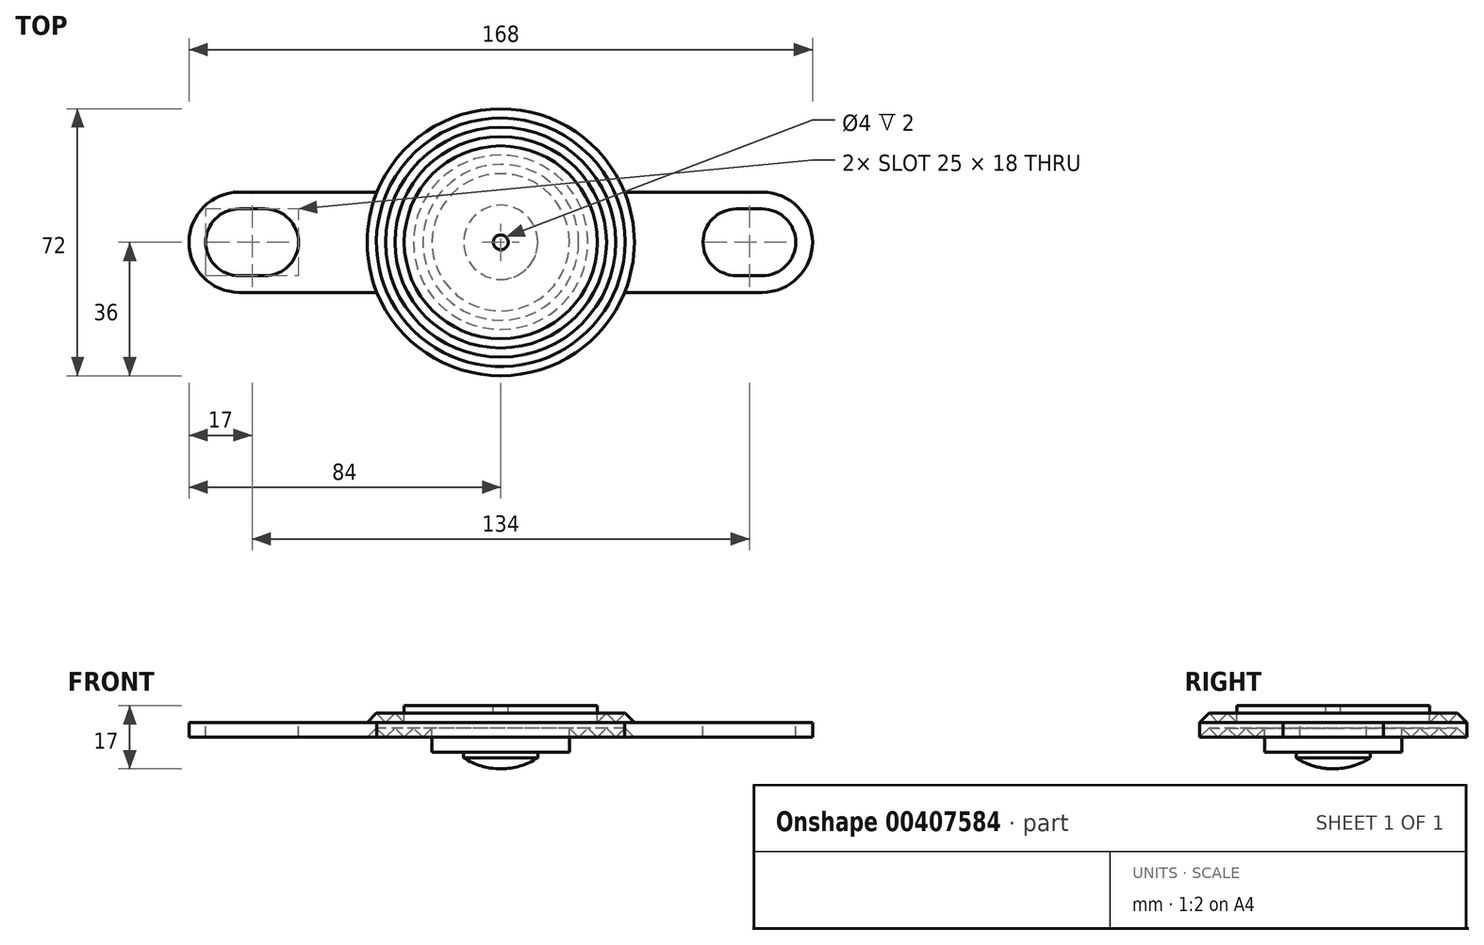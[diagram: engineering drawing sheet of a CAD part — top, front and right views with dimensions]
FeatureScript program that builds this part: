
annotation { "Feature Type Name" : "Feature", "Feature Type Description" : "" }
export const myFeature = defineFeature(function(context is Context, id is Id, definition is map)
    precondition{}
    {
        {
            var Q0;
            Q0=qCreatedBy(makeId("Right.planeOp"),FACE);
            var sketch = newSketch(context, id + "F0", { "sketchPlane" : qUnion([Q0])});
            skLineSegment(sketch, "E0", {"start": v(0, 21.06) * mm, "end": v(0, -33.67) * mm, "construction": true});
            skLineSegment(sketch, "E1", {"start": v(2, 0) * mm, "end": v(26, 0) * mm});
            skLineSegment(sketch, "E2", {"start": v(26, 0) * mm, "end": v(26, -4.5) * mm});
            skLineSegment(sketch, "E3", {"start": v(26, -4.5) * mm, "end": v(28.5, -2) * mm});
            skLineSegment(sketch, "E4", {"start": v(28.5, -2) * mm, "end": v(31, -4.5) * mm});
            skLineSegment(sketch, "E5", {"start": v(31, -4.5) * mm, "end": v(33.5, -2) * mm});
            skLineSegment(sketch, "E6", {"start": v(33.5, -2) * mm, "end": v(36, -4.5) * mm});
            skLineSegment(sketch, "E7", {"start": v(36, -4.5) * mm, "end": v(36, -8.5) * mm});
            skLineSegment(sketch, "E8", {"start": v(36, -8.5) * mm, "end": v(33.5, -6) * mm});
            skLineSegment(sketch, "E9", {"start": v(33.5, -6) * mm, "end": v(31, -8.5) * mm});
            skLineSegment(sketch, "E10", {"start": v(31, -8.5) * mm, "end": v(28.5, -6) * mm});
            skLineSegment(sketch, "E11", {"start": v(28.5, -6) * mm, "end": v(26, -8.5) * mm});
            skLineSegment(sketch, "E12", {"start": v(26, -8.5) * mm, "end": v(23.5, -6) * mm});
            skLineSegment(sketch, "E13", {"start": v(23.5, -6) * mm, "end": v(21, -8.5) * mm});
            skLineSegment(sketch, "E14", {"start": v(21, -8.5) * mm, "end": v(18.5, -6) * mm});
            skLineSegment(sketch, "E15", {"start": v(18.5, -6) * mm, "end": v(18.5, -12.5) * mm});
            skLineSegment(sketch, "E16", {"start": v(18.5, -12.5) * mm, "end": v(10, -12.5) * mm});
            skLineSegment(sketch, "E17", {"start": v(10, -12.5) * mm, "end": v(10, -14) * mm});
            skLineSegment(sketch, "E18", {"start": v(10, -14) * mm, "end": v(0, -14) * mm});
            skLineSegment(sketch, "E19", {"start": v(0, -14) * mm, "end": v(0, 0) * mm});
            skArc(sketch, "E20", {"start": v(0, -17) * mm, "mid": v(5.22, -16.23) * mm, "end": v(10, -14) * mm});
            skLineSegment(sketch, "E21", {"start": v(2, 0) * mm, "end": v(2, -2) * mm});
            skLineSegment(sketch, "E22", {"start": v(2, -2) * mm, "end": v(0, -2) * mm});
            skLineSegment(sketch, "E23", {"start": v(0, -14) * mm, "end": v(0, -17) * mm});
            skSolve(sketch);
        }
        {
            var Q0;
            Q0=makeQuery(id+"F0.imprint","IMPRINT",FACE,{"disambiguationData":[TD([[makeQuery(id+"F0.imprint","IMPRINT",EDGE,{"derivedFrom":sQuery(id+"F0.wireOp",EDGE,"E1")}),-1.0]])]});
            var Q1;
            Q1=makeQuery(id+"F0.imprint","IMPRINT",FACE,{"disambiguationData":[TD([[makeQuery(id+"F0.imprint","IMPRINT",EDGE,{"derivedFrom":sQuery(id+"F0.wireOp",EDGE,"E18")}),1.0]])]});
            var Q2;
            Q2=sQuery(id+"F0.wireOp",EDGE,"E0");
            revolve(context, id + "F1", {"entities" : qUnion([Q0, Q1]), "axis" : qUnion([Q2]), "revolveType" : RevolveType.FULL});
        }
        {
            var Q0;
            Q0=makeQuery(id+"F1.opRevolve","SWEPT_FACE",FACE,{"disambiguationData":[OSD([sQuery(id+"F0.wireOp",EDGE,"E1")])]});
            var sketch = newSketch(context, id + "F2", { "sketchPlane" : qUnion([Q0])});
            skLineSegment(sketch, "E24", {"start": v(-33.2, 13.5) * mm, "end": v(-70.5, 13.5) * mm});
            skLineSegment(sketch, "E25", {"start": v(-70.5, -13.5) * mm, "end": v(-33.2, -13.5) * mm});
            skArc(sketch, "E26", {"start": v(-33.2, 13.5) * mm, "mid": v(-36, 0) * mm, "end": v(-33.2, -13.5) * mm});
            skLineSegment(sketch, "E27", {"start": v(-129.3, 0) * mm, "end": v(127.45, 0) * mm, "construction": true});
            skLineSegment(sketch, "E28", {"start": v(-46.2, 0) * mm, "end": v(-46.2, 13.5) * mm, "construction": true});
            skLineSegment(sketch, "E29", {"start": v(-46.2, 0) * mm, "end": v(-46.2, -13.5) * mm, "construction": true});
            skArc(sketch, "E30", {"start": v(-70.5, 13.5) * mm, "mid": v(-84, 0) * mm, "end": v(-70.5, -13.5) * mm});
            skPoint(sketch, "E31", {"position": v(-36, 0) * mm});
            skPoint(sketch, "E32", {"position": v(-84, 0) * mm});
            skCircle(sketch, "E33", {"center": v(-70.5, 0) * mm, "radius": 9 * mm});
            skCircle(sketch, "E34", {"center": v(-63.5, 0) * mm, "radius": 9 * mm});
            skLineSegment(sketch, "E35", {"start": v(-70.5, 9) * mm, "end": v(-63.5, 9) * mm});
            skLineSegment(sketch, "E36", {"start": v(-70.5, -9) * mm, "end": v(-63.5, -9) * mm});
            skLineSegment(sketch, "E37", {"start": v(0, 37.91) * mm, "end": v(0, -41.04) * mm, "construction": true});
            skPoint(sketch, "E38.MirrorP", {"position": v(84, 0) * mm});
            skLineSegment(sketch, "E39.MirrorCS", {"start": v(70.5, 9) * mm, "end": v(63.5, 9) * mm});
            skPoint(sketch, "E40.MirrorP", {"position": v(36, 0) * mm});
            skCircle(sketch, "E41.MirrorC", {"center": v(70.5, 0) * mm, "radius": 9 * mm});
            skLineSegment(sketch, "E42.MirrorCS", {"start": v(70.5, -13.5) * mm, "end": v(33.2, -13.5) * mm});
            skCircle(sketch, "E43.MirrorC", {"center": v(63.5, 0) * mm, "radius": 9 * mm});
            skLineSegment(sketch, "E44.MirrorCS", {"start": v(46.2, 0) * mm, "end": v(46.2, -13.5) * mm, "construction": true});
            skLineSegment(sketch, "E45.MirrorCS", {"start": v(46.2, 0) * mm, "end": v(46.2, 13.5) * mm, "construction": true});
            skLineSegment(sketch, "E46.MirrorCS", {"start": v(33.2, 13.5) * mm, "end": v(70.5, 13.5) * mm});
            skArc(sketch, "E47.MirrorCS", {"start": v(33.2, 13.5) * mm, "mid": v(36, 0) * mm, "end": v(33.2, -13.5) * mm});
            skLineSegment(sketch, "E48.MirrorCS", {"start": v(70.5, -9) * mm, "end": v(63.5, -9) * mm});
            skArc(sketch, "E49.MirrorCS", {"start": v(70.5, 13.5) * mm, "mid": v(84, 0) * mm, "end": v(70.5, -13.5) * mm});
            skSolve(sketch);
        }
        {
            var Q0;
            Q0=makeQuery(id+"F2.imprint","IMPRINT",FACE,{"disambiguationData":[TD([[makeQuery(id+"F2.imprint","IMPRINT",EDGE,{"derivedFrom":sQuery(id+"F2.wireOp",EDGE,"E24")}),1.0]])]});
            var Q1;
            {var subQ1=sQuery(id+"F2.wireOp",EDGE,"E39.MirrorCS");Q1=makeQuery(id+"F2.imprint","IMPRINT",FACE,{"disambiguationData":[TD([[makeQuery(id+"F2.imprint","IMPRINT",EDGE,{"derivedFrom":subQ1}),-1.0]])]});}
            extrude(context, id + "F3", {"entities" : qUnion([Q0, Q1]), "operationType" : NewBodyOperationType.ADD, "oppositeDirection" : true, "depth" : 8.5 * mm, "hasSecondDirection" : true, "secondDirectionOppositeDirection" : true, "secondDirectionDepth" : 4.5 * mm});
        }
    });
